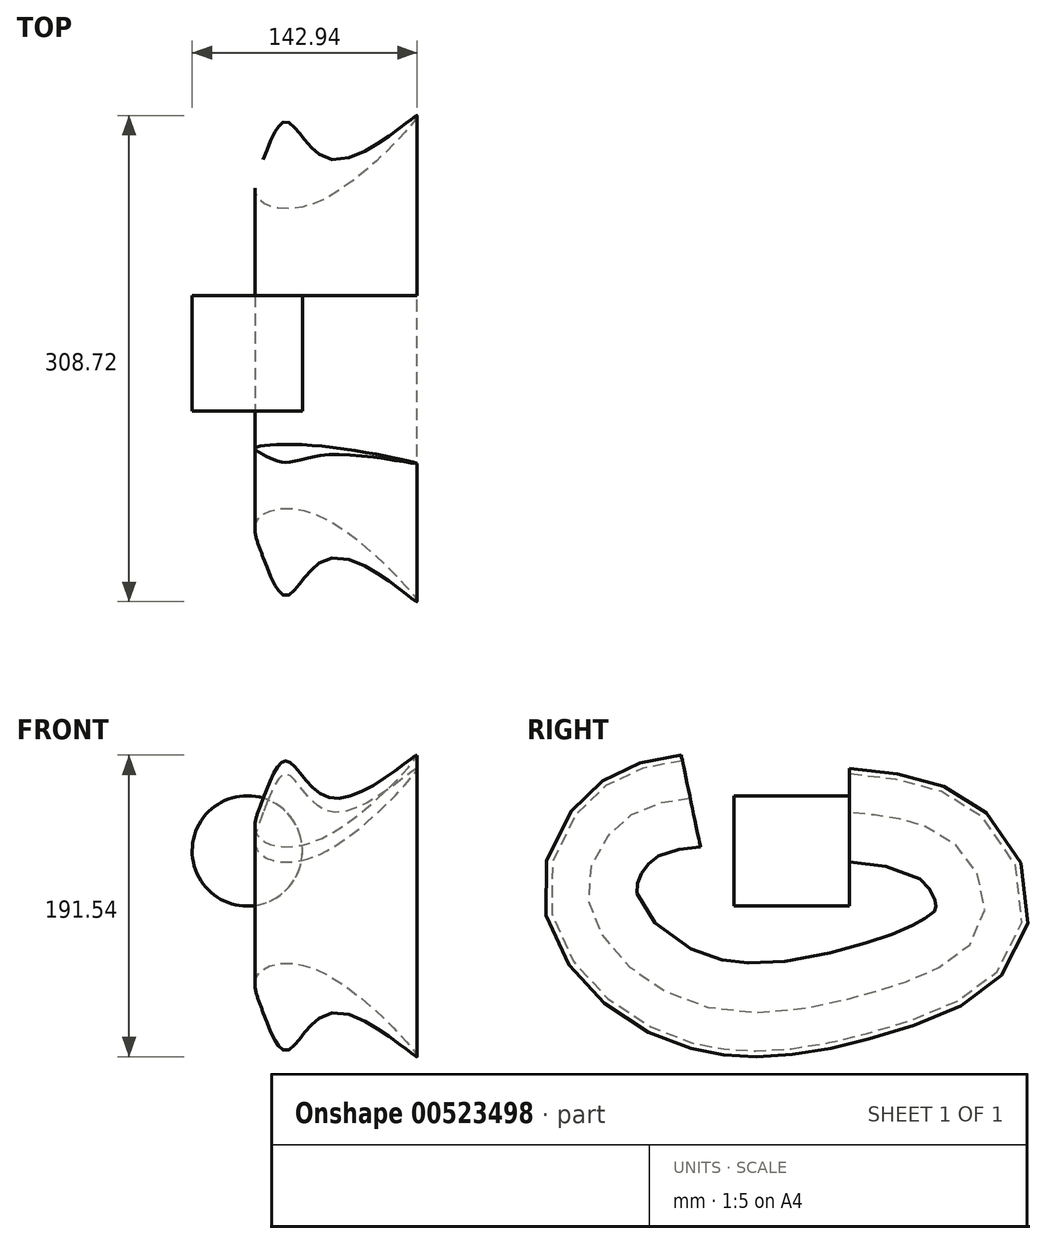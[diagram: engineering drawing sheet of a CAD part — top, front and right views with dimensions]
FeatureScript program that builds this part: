
annotation { "Feature Type Name" : "Feature", "Feature Type Description" : "" }
export const myFeature = defineFeature(function(context is Context, id is Id, definition is map)
    precondition{}
    {
        {
            var Q0;
            Q0=qCreatedBy(makeId("Front.planeOp"),FACE);
            var sketch = newSketch(context, id + "F0", { "sketchPlane" : qUnion([Q0])});
            skCircle(sketch, "E0", {"center": v(-25.09, -24.42) * mm, "radius": 35 * mm});
            skPoint(sketch, "E0.first.point", {"position": v(-24.3, -59.42) * mm});
            skPoint(sketch, "E0.second.point", {"position": v(-29.43, 10.32) * mm});
            skPoint(sketch, "E0.third.point", {"position": v(0, 0) * mm});
            skSolve(sketch);
        }
        {
            var Q0;
            Q0=makeQuery(id+"F0.imprint","IMPRINT",FACE,{"disambiguationData":[TD([[makeQuery(id+"F0.imprint","IMPRINT",EDGE,{"derivedFrom":sQuery(id+"F0.wireOp",EDGE,"E0")}),1.0]])]});
            extrude(context, id + "F1", {"entities" : qUnion([Q0]), "depth" : 73.25 * mm, "offsetDistance" : 25.4 * mm});
        }
        {
            var Q0;
            Q0=qCreatedBy(makeId("Right.planeOp"),FACE);
            var sketch = newSketch(context, id + "F2", { "sketchPlane" : qUnion([Q0])});
            skFitSpline(sketch, "E1", {"points": [v(0, -9.16) * mm, v(60.1, -25.96) * mm, v(75.37, -69.14) * mm, v(9.72, -106.22) * mm, v(-97.6, -112.11) * mm, v(-156.93, -54.1) * mm, v(-135.77, -10.69) * mm, v(-99.12, 0) * mm], "startDerivative": vector(477.08, -44.93) * mm, "endDerivative": vector(344.36, 38.9) * mm});
            skSolve(sketch);
        }
        {
            var Q0;
            Q0=qCreatedBy(makeId("Front.planeOp"),FACE);
            var sketch = newSketch(context, id + "F3", { "sketchPlane" : qUnion([Q0])});
            skFitSpline(sketch, "E2", {"points": [v(-14.98, 0) * mm, v(-18.73, -23.84) * mm, v(22.2, -25.98) * mm, v(82.67, 28.06) * mm, v(29.96, 0) * mm, v(0, 24.32) * mm, v(-14.98, 0) * mm]});
            skSolve(sketch);
        }
        {
            var Q0;
            Q0 = qSketchRegion(id + "F3", true);
            var Q1;
            Q1 = qBodyType(qCreatedBy(id + "F2" ,EDGE), BodyType.WIRE);
            sweep(context, id + "F4", {"operationType" : NewBodyOperationType.ADD, "profiles" : qUnion([Q0]), "path" : qUnion([Q1])});
        }
    });
